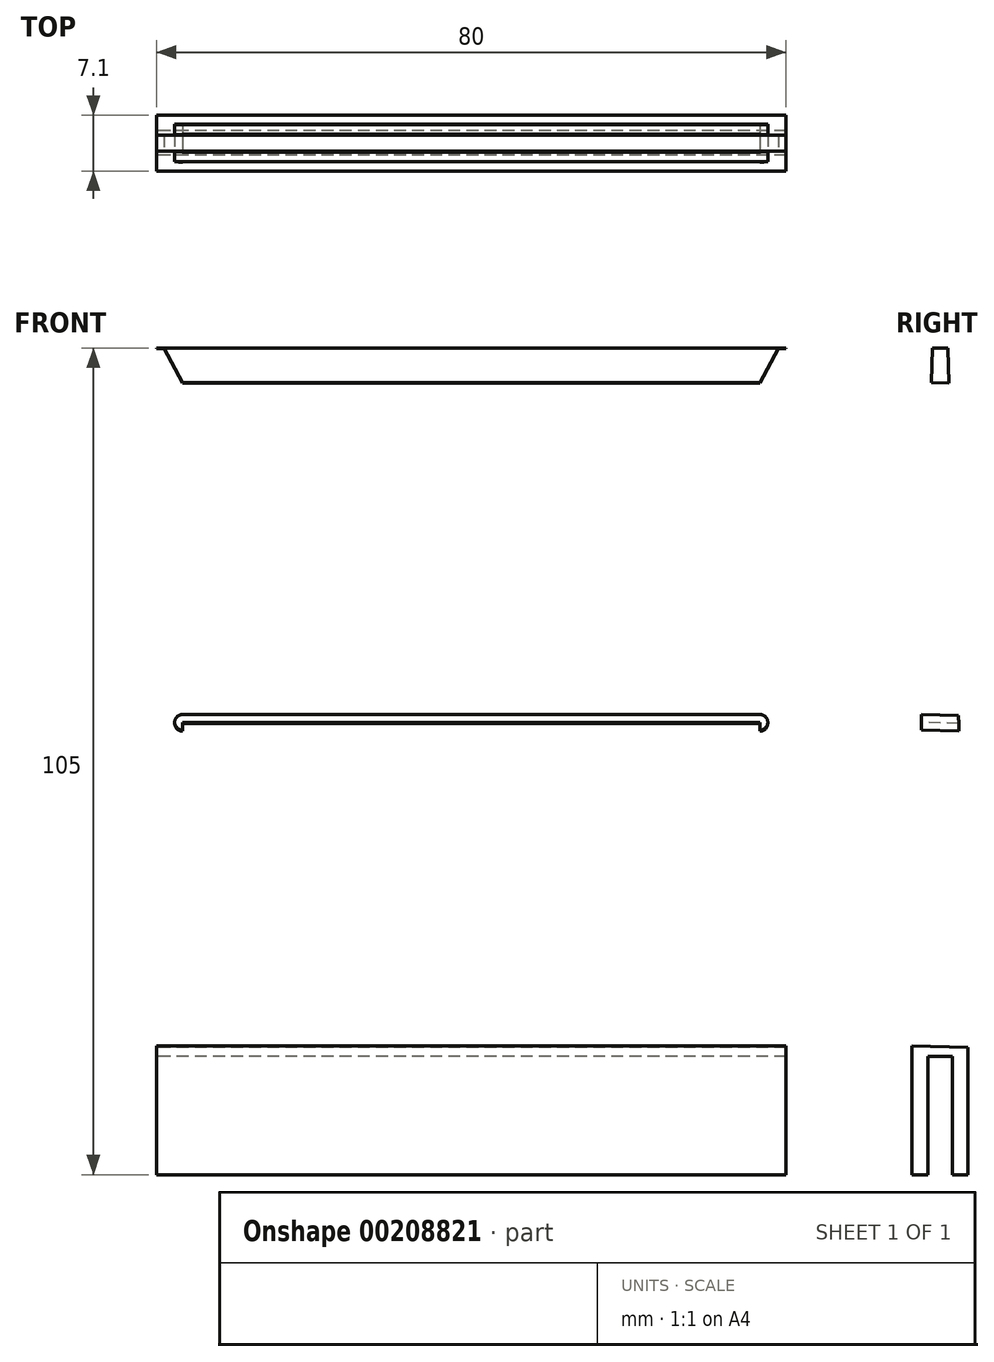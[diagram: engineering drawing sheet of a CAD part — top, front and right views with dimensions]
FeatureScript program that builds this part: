
annotation { "Feature Type Name" : "Feature", "Feature Type Description" : "" }
export const myFeature = defineFeature(function(context is Context, id is Id, definition is map)
    precondition{}
    {
        {
            var Q0;
            Q0=qCreatedBy(makeId("Right.planeOp"),FACE);
            var sketch = newSketch(context, id + "F0", { "sketchPlane" : qUnion([Q0])});
            skLineSegment(sketch, "E0", {"start": v(-1.55, 0) * mm, "end": v(1.55, 0) * mm});
            skLineSegment(sketch, "E1", {"start": v(1.55, 0) * mm, "end": v(1.55, -15) * mm});
            skLineSegment(sketch, "E2", {"start": v(1.55, -15) * mm, "end": v(3.55, -15) * mm});
            skLineSegment(sketch, "E3", {"start": v(3.55, -15) * mm, "end": v(3.55, 1.36) * mm});
            skLineSegment(sketch, "E4", {"start": v(3.55, 1.36) * mm, "end": v(1, 90) * mm});
            skLineSegment(sketch, "E5", {"start": v(1, 90) * mm, "end": v(-1, 90) * mm});
            skLineSegment(sketch, "E6", {"start": v(-1, 90) * mm, "end": v(-3.55, 1.36) * mm});
            skLineSegment(sketch, "E7", {"start": v(-3.55, 1.36) * mm, "end": v(-3.55, 0) * mm});
            skLineSegment(sketch, "E8", {"start": v(-3.55, 0) * mm, "end": v(-3.55, -15) * mm});
            skLineSegment(sketch, "E9", {"start": v(-3.55, -15) * mm, "end": v(-1.55, -15) * mm});
            skLineSegment(sketch, "E10", {"start": v(-1.55, -15) * mm, "end": v(-1.55, 0) * mm});
            skSolve(sketch);
        }
        {
            var Q0;
            Q0=makeQuery(id+"F0.imprint","IMPRINT",FACE,{"disambiguationData":[TD([[makeQuery(id+"F0.imprint","IMPRINT",EDGE,{"derivedFrom":sQuery(id+"F0.wireOp",EDGE,"E0")}),1.0]])]});
            extrude(context, id + "F1", {"entities" : qUnion([Q0]), "depth" : 80 * mm, "symmetric" : true});
        }
        {
            var Q0;
            Q0=makeQuery(id+"F1.opExtrude","SWEPT_FACE",FACE,{"disambiguationData":[OSD([sQuery(id+"F0.wireOp",EDGE,"E6")])]});
            var sketch = newSketch(context, id + "F2", { "sketchPlane" : qUnion([Q0])});
            skLineSegment(sketch, "E11.0", {"start": v(40, 89.93) * mm, "end": v(-40, 89.93) * mm});
            skLineSegment(sketch, "E12", {"start": v(-39.05, 89.93) * mm, "end": v(-36.67, 85.53) * mm});
            skLineSegment(sketch, "E13", {"start": v(-36.67, 85.53) * mm, "end": v(36.67, 85.53) * mm});
            skLineSegment(sketch, "E14", {"start": v(36.67, 85.53) * mm, "end": v(39.05, 89.93) * mm});
            skLineSegment(sketch, "E15", {"start": v(-39.05, 89.93) * mm, "end": v(-40, 89.93) * mm});
            skLineSegment(sketch, "E16", {"start": v(39.05, 89.93) * mm, "end": v(40, 89.93) * mm});
            skLineSegment(sketch, "E17.bottom", {"start": v(-36.67, 82.2) * mm, "end": v(36.67, 82.2) * mm});
            skLineSegment(sketch, "E17.top", {"start": v(-36.67, 2.58) * mm, "end": v(36.67, 2.58) * mm});
            skLineSegment(sketch, "E17.left", {"start": v(-36.67, 82.2) * mm, "end": v(-36.67, 2.58) * mm});
            skLineSegment(sketch, "E17.right", {"start": v(36.67, 82.2) * mm, "end": v(36.67, 2.58) * mm});
            skArc(sketch, "E18.0.startCap", {"start": v(-37.4, 81.52) * mm, "mid": v(-37.34, 82.93) * mm, "end": v(-35.93, 82.87) * mm});
            skArc(sketch, "E18.0.endCap", {"start": v(37.4, 3.26) * mm, "mid": v(37.34, 1.84) * mm, "end": v(35.93, 1.9) * mm});
            skArc(sketch, "E19.0.startCap", {"start": v(35.93, 82.87) * mm, "mid": v(37.34, 82.93) * mm, "end": v(37.4, 81.52) * mm});
            skArc(sketch, "E19.0.endCap", {"start": v(-35.93, 1.9) * mm, "mid": v(-37.34, 1.84) * mm, "end": v(-37.4, 3.26) * mm});
            skPoint(sketch, "E20", {"position": v(36.67, 42.39) * mm});
            skPoint(sketch, "E21", {"position": v(-36.67, 42.39) * mm});
            skLineSegment(sketch, "E22", {"start": v(36.67, 42.39) * mm, "end": v(-36.67, 42.39) * mm});
            skArc(sketch, "E23.0.startCap", {"start": v(36.67, 43.39) * mm, "mid": v(37.67, 42.39) * mm, "end": v(36.67, 41.39) * mm});
            skArc(sketch, "E23.0.endCap", {"start": v(-36.67, 41.39) * mm, "mid": v(-37.67, 42.39) * mm, "end": v(-36.67, 43.39) * mm});
            skLineSegment(sketch, "E23.0.left", {"start": v(36.67, 41.39) * mm, "end": v(-36.67, 41.39) * mm});
            skLineSegment(sketch, "E23.0.right", {"start": v(36.67, 43.39) * mm, "end": v(-36.67, 43.39) * mm});
            skSolve(sketch);
        }
        {
            var Q0;
            Q0=makeQuery(id+"F2.imprint","IMPRINT",FACE,{"disambiguationData":[TD([[makeQuery(id+"F2.imprint","IMPRINT",EDGE,{"derivedFrom":sQuery(id+"F2.wireOp",EDGE,"E11.0")}),1.0]])]});
            var Q1;
            Q1=makeQuery(id+"F2.imprint","IMPRINT",FACE,{"disambiguationData":[TD([[makeQuery(id+"F2.imprint","IMPRINT",EDGE,{"derivedFrom":sQuery(id+"F2.wireOp",EDGE,"E17.bottom")}),-1.0]])]});
            var Q2;
            {var subQ0=sQuery(id+"F2.wireOp",EDGE,"E19.0.left");var subQ1=sQuery(id+"F2.wireOp",EDGE,"E17.right");var subQ2=makeQuery(id+"F2.imprint","INTERSECT",VERTEX,{"derivedFrom":[subQ1,subQ0]});Q2=makeQuery(id+"F2.imprint","IMPRINT",FACE,{"disambiguationData":[TD([[makeQuery(id+"F2.imprint","IMPRINT",EDGE,{"disambiguationData":[TD([[subQ2,-1.0]])],"derivedFrom":subQ1}),-1.0]])]});}
            var Q3;
            {var subQ0=sQuery(id+"F2.wireOp",EDGE,"E19.0.left");var subQ1=sQuery(id+"F2.wireOp",EDGE,"E17.top");var subQ2=makeQuery(id+"F2.imprint","INTERSECT",VERTEX,{"derivedFrom":[subQ1,subQ0]});Q3=makeQuery(id+"F2.imprint","IMPRINT",FACE,{"disambiguationData":[TD([[makeQuery(id+"F2.imprint","IMPRINT",EDGE,{"disambiguationData":[TD([[subQ2,-1.0]])],"derivedFrom":subQ1}),1.0]])]});}
            var Q4;
            {var subQ0=sQuery(id+"F2.wireOp",EDGE,"E18.0.right");var subQ1=sQuery(id+"F2.wireOp",EDGE,"E17.left");var subQ2=makeQuery(id+"F2.imprint","INTERSECT",VERTEX,{"derivedFrom":[subQ1,subQ0]});Q4=makeQuery(id+"F2.imprint","IMPRINT",FACE,{"disambiguationData":[TD([[makeQuery(id+"F2.imprint","IMPRINT",EDGE,{"disambiguationData":[TD([[subQ2,-1.0]])],"derivedFrom":subQ1}),1.0]])]});}
            extrude(context, id + "F3", {"entities" : qUnion([Q0, Q1, Q2, Q3, Q4]), "operationType" : NewBodyOperationType.REMOVE, "endBound" : BoundingType.THROUGH_ALL, "oppositeDirection" : true, "depth" : 25 * mm});
        }
    });
